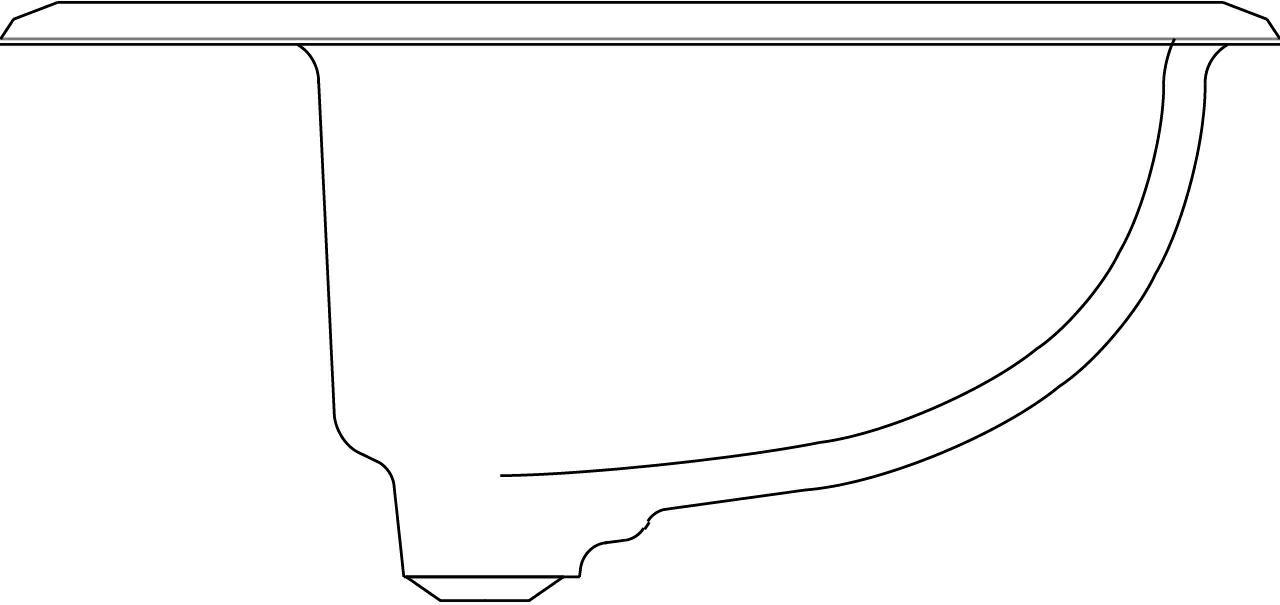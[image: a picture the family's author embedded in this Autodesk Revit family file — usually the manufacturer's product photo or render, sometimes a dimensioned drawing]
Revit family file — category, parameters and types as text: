
# Revit family: 62-LVM NOVARA INCRUS
name_source: partatom
category: Aparatos sanitarios
revit_build: Autodesk Revit 2018 (Build: 20170223_1515(x64)
units: mm (PartAtom-declared; Revit-internal decimal feet)

## family parameters
Anfitrión = Cara
Compartido = No
Corte con vacíos al cargar = No
Cota de conector redondo = Diámetro de uso
Número OmniClass = 23.45.55.00
Punto de cálculo de habitación = No
Tipo de pieza = Normal
Título OmniClass = Sanitary Faucets, Wastes

## types (1)
- 62-LVM NOVARA INCRUS
    Acabado = Brillante
    Altura Nominal = 26.5 mm
    Ancho Nominal = 343 mm
    Características = Permite instalar con grifería a la pared  o en el mesón, agujero integral de drenaje que evita el rebosa, amplio pozo
    Color = Blanco
    Cumplimiento de Norma = Normas NTC 920 y ANSI-ASME A112.19.2., cumple requerimientos ADA para accesibilidad
    Descripción = Diseño contemporaneo, que permite combinar con gran cantidad de sanitarios, Agujero integral de drenaje que evita el rebose, Agujeros insinuados que permiten escoger diferentes opciones de griferia
    Descripción IFC = Novara incrustar Lavamanos de incrustar en porcelana sanitaria
    Descripción de la garantía = Porcelana sanitaria garantía de por vida, garantía de 5 años para grifería
    Duración Garantía Partes = Integral de por vida
    Elevación por defecto = 1219 mm
    Fabricante = www.corona.com.co
    Forma = Rectangular
    Imagen de tipo = <Ninguno>
    Información del producto = https://corona.co
    Logitud Nominal = 535 mm
    Material = Ceramica_Corona_Blanco
    Material de Fabricacion = Porcelana Sanitaria
    Nombre = Lavamanos Novara
    Nombre del Fabricante = CORONA
    Número Modelo = 01301
    Requerimiento de Accesibilidad = Manual
    Responsable Garantías Partes = www.corona.com.co
    Tamaño = 535 x 343 x 26,5 mm
    Tipo de Activo = Fijo
    Tráfico = Residencial
    URL = https://www.corona.co
